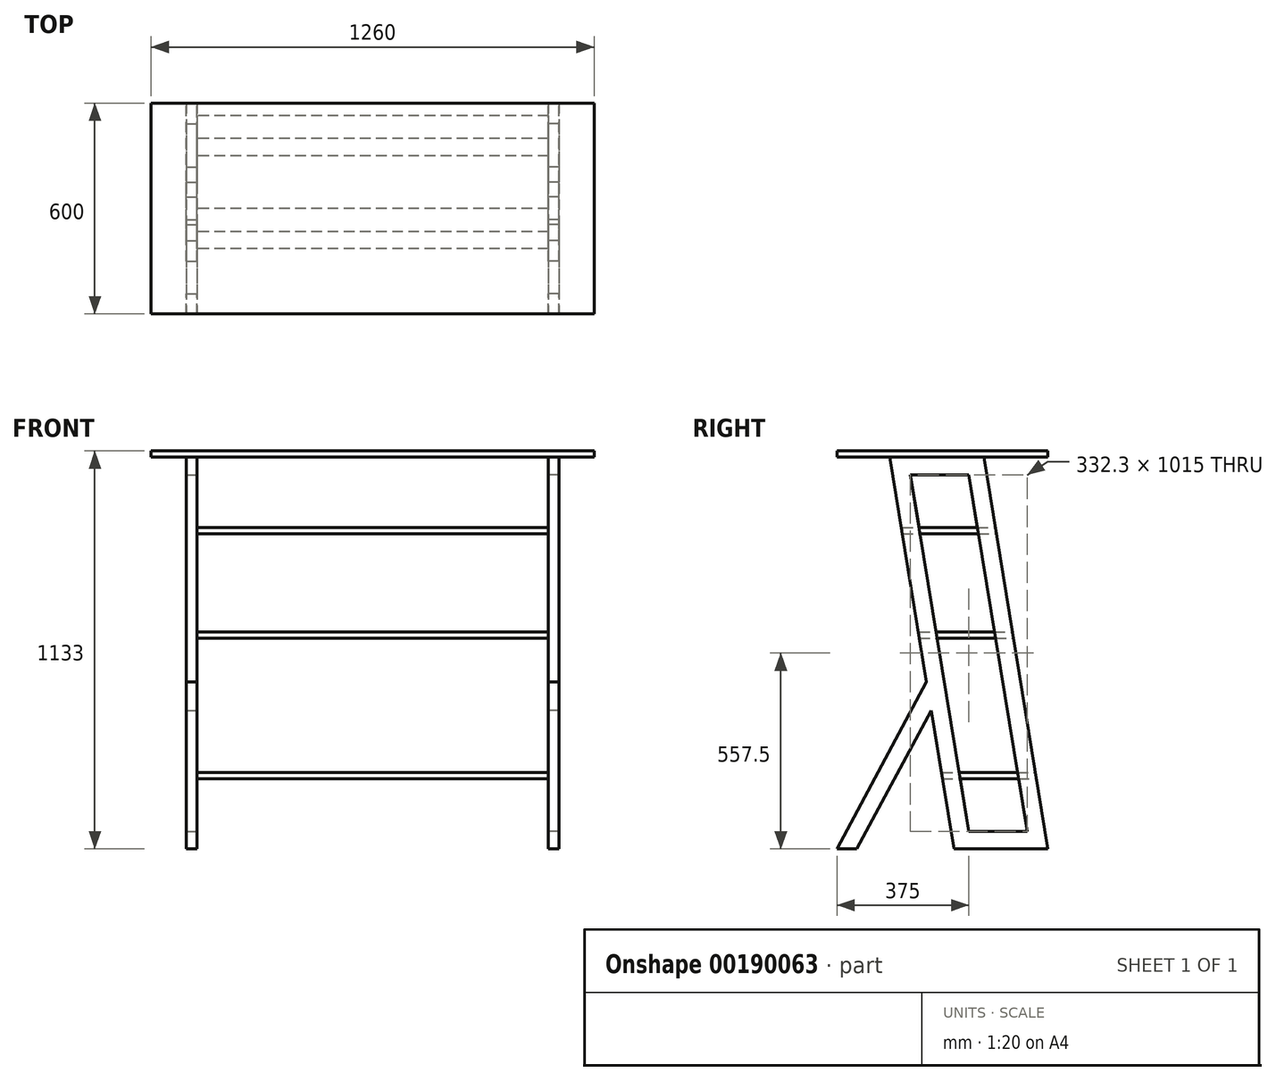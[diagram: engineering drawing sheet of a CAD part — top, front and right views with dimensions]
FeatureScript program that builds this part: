
annotation { "Feature Type Name" : "Feature", "Feature Type Description" : "" }
export const myFeature = defineFeature(function(context is Context, id is Id, definition is map)
    precondition{}
    {
        {
            var Q0;
            Q0=qCreatedBy(makeId("Right.planeOp"),FACE);
            cPlane(context, id + "F0", {"entities" : qUnion([Q0]), "cplaneType" : CPlaneType.OFFSET, "offset" : 500 * mm, "width" : 150 * mm, "height" : 150 * mm});
        }
        {
            var Q0;
            Q0=qCreatedBy(id+"F0.planeOp",FACE);
            var sketch = newSketch(context, id + "F1", { "sketchPlane" : qUnion([Q0])});
            skLineSegment(sketch, "E0", {"start": v(-331.97, 393.95) * mm, "end": v(-543.26, 0) * mm});
            skLineSegment(sketch, "E1", {"start": v(-600, 0) * mm, "end": v(-543.26, 0) * mm});
            skLineSegment(sketch, "E2", {"start": v(-345.24, 475) * mm, "end": v(-600, 0) * mm});
            skLineSegment(sketch, "E3", {"start": v(-331.97, 393.95) * mm, "end": v(-267.48, 0) * mm});
            skLineSegment(sketch, "E4", {"start": v(-267.48, 0) * mm, "end": v(0, 0) * mm});
            skLineSegment(sketch, "E5", {"start": v(0, 0) * mm, "end": v(-182.52, 1115) * mm});
            skLineSegment(sketch, "E6", {"start": v(-182.52, 1115) * mm, "end": v(-450, 1115) * mm});
            skLineSegment(sketch, "E7", {"start": v(-450, 1115) * mm, "end": v(-345.24, 475) * mm});
            skLineSegment(sketch, "E8", {"start": v(-391.15, 1065) * mm, "end": v(-225, 50) * mm});
            skLineSegment(sketch, "E9", {"start": v(-225, 50) * mm, "end": v(-58.85, 50) * mm});
            skLineSegment(sketch, "E10", {"start": v(-58.85, 50) * mm, "end": v(-225, 1065) * mm});
            skLineSegment(sketch, "E11", {"start": v(-225, 1065) * mm, "end": v(-391.15, 1065) * mm});
            skLineSegment(sketch, "E12", {"start": v(-450, 1115) * mm, "end": v(-450, 0) * mm, "construction": true});
            skLineSegment(sketch, "E13", {"start": v(-450, 0) * mm, "end": v(-267.48, 0) * mm, "construction": true});
            skLineSegment(sketch, "E14", {"start": v(-450, 1115) * mm, "end": v(-600, 1115) * mm, "construction": true});
            skLineSegment(sketch, "E15", {"start": v(-600, 1115) * mm, "end": v(-600, 0) * mm, "construction": true});
            skLineSegment(sketch, "E16", {"start": v(-543.26, 0) * mm, "end": v(-450, 0) * mm, "construction": true});
            skSolve(sketch);
        }
        {
            var Q0;
            Q0 = qSketchRegion(id + "F1", true);
            extrude(context, id + "F2", {"entities" : qUnion([Q0]), "depth" : 30 * mm});
        }
        {
            var Q0;
            Q0=qCreatedBy(makeId("Front.planeOp"),FACE);
            var sketch = newSketch(context, id + "F3", { "sketchPlane" : qUnion([Q0])});
            skLineSegment(sketch, "E17.bottom", {"start": v(0, 1133) * mm, "end": v(630, 1133) * mm});
            skLineSegment(sketch, "E17.top", {"start": v(0, 1115) * mm, "end": v(630, 1115) * mm});
            skLineSegment(sketch, "E17.left", {"start": v(0, 1133) * mm, "end": v(0, 1115) * mm});
            skLineSegment(sketch, "E17.right", {"start": v(630, 1133) * mm, "end": v(630, 1115) * mm});
            skSolve(sketch);
        }
        {
            var Q0;
            Q0 = qSketchRegion(id + "F3", true);
            extrude(context, id + "F4", {"entities" : qUnion([Q0]), "operationType" : NewBodyOperationType.ADD, "depth" : 600 * mm});
        }
        {
            var Q0;
            Q0=qCreatedBy(makeId("Right.planeOp"),FACE);
            var sketch = newSketch(context, id + "F5", { "sketchPlane" : qUnion([Q0])});
            skLineSegment(sketch, "E18.bottom", {"start": v(-414.31, 915) * mm, "end": v(-149.78, 915) * mm});
            skLineSegment(sketch, "E18.top", {"start": v(-414.31, 897) * mm, "end": v(-149.78, 897) * mm});
            skLineSegment(sketch, "E18.left", {"start": v(-414.31, 915) * mm, "end": v(-414.31, 897) * mm});
            skLineSegment(sketch, "E18.right", {"start": v(-149.78, 915) * mm, "end": v(-149.78, 897) * mm});
            skLineSegment(sketch, "E19.bottom", {"start": v(-365.7, 618) * mm, "end": v(-101.16, 618) * mm});
            skLineSegment(sketch, "E19.top", {"start": v(-365.7, 600) * mm, "end": v(-101.16, 600) * mm});
            skLineSegment(sketch, "E19.left", {"start": v(-365.7, 618) * mm, "end": v(-365.7, 600) * mm});
            skLineSegment(sketch, "E19.right", {"start": v(-101.16, 618) * mm, "end": v(-101.16, 600) * mm});
            skLineSegment(sketch, "E20.bottom", {"start": v(-300.22, 218) * mm, "end": v(-35.69, 218) * mm});
            skLineSegment(sketch, "E20.top", {"start": v(-300.22, 200) * mm, "end": v(-35.69, 200) * mm});
            skLineSegment(sketch, "E20.left", {"start": v(-300.22, 218) * mm, "end": v(-300.22, 200) * mm});
            skLineSegment(sketch, "E20.right", {"start": v(-35.69, 218) * mm, "end": v(-35.69, 200) * mm});
            skSolve(sketch);
        }
        {
            var Q0;
            Q0 = qSketchRegion(id + "F5", true);
            var Q1;
            Q1=makeQuery(id+"F2.opExtrude","CAP_FACE",FACE,{"disambiguationData":[OSD([sQuery(id+"F1.wireOp",EDGE,"E0"),sQuery(id+"F1.wireOp",EDGE,"E1"),sQuery(id+"F1.wireOp",EDGE,"E2"),sQuery(id+"F1.wireOp",EDGE,"E3"),sQuery(id+"F1.wireOp",EDGE,"E4"),sQuery(id+"F1.wireOp",EDGE,"E5"),sQuery(id+"F1.wireOp",EDGE,"E6"),sQuery(id+"F1.wireOp",EDGE,"E7"),sQuery(id+"F1.wireOp",EDGE,"E8"),sQuery(id+"F1.wireOp",EDGE,"E9"),sQuery(id+"F1.wireOp",EDGE,"E10"),sQuery(id+"F1.wireOp",EDGE,"E11")])],"isStart":true});
            extrude(context, id + "F6", {"entities" : qUnion([Q0]), "operationType" : NewBodyOperationType.ADD, "endBound" : BoundingType.UP_TO_SURFACE, "endBoundEntityFace" : qUnion([Q1]), "depth" : 25 * mm});
        }
        {
            var Q0;
            Q0=makeQuery(id+"F2.opExtrude","SWEPT_BODY",BODY,{"disambiguationData":[OSD([sQuery(id+"F1.wireOp",EDGE,"E0"),sQuery(id+"F1.wireOp",EDGE,"E1"),sQuery(id+"F1.wireOp",EDGE,"E2"),sQuery(id+"F1.wireOp",EDGE,"E3"),sQuery(id+"F1.wireOp",EDGE,"E4"),sQuery(id+"F1.wireOp",EDGE,"E5"),sQuery(id+"F1.wireOp",EDGE,"E6"),sQuery(id+"F1.wireOp",EDGE,"E7"),sQuery(id+"F1.wireOp",EDGE,"E8"),sQuery(id+"F1.wireOp",EDGE,"E9"),sQuery(id+"F1.wireOp",EDGE,"E10"),sQuery(id+"F1.wireOp",EDGE,"E11")])]});
            var Q1;
            Q1=qCreatedBy(makeId("Right.planeOp"),FACE);
            mirror(context, id + "F7", {"operationType" : NewBodyOperationType.ADD, "entities" : qUnion([Q0]), "mirrorPlane" : qUnion([Q1])});
        }
    });
